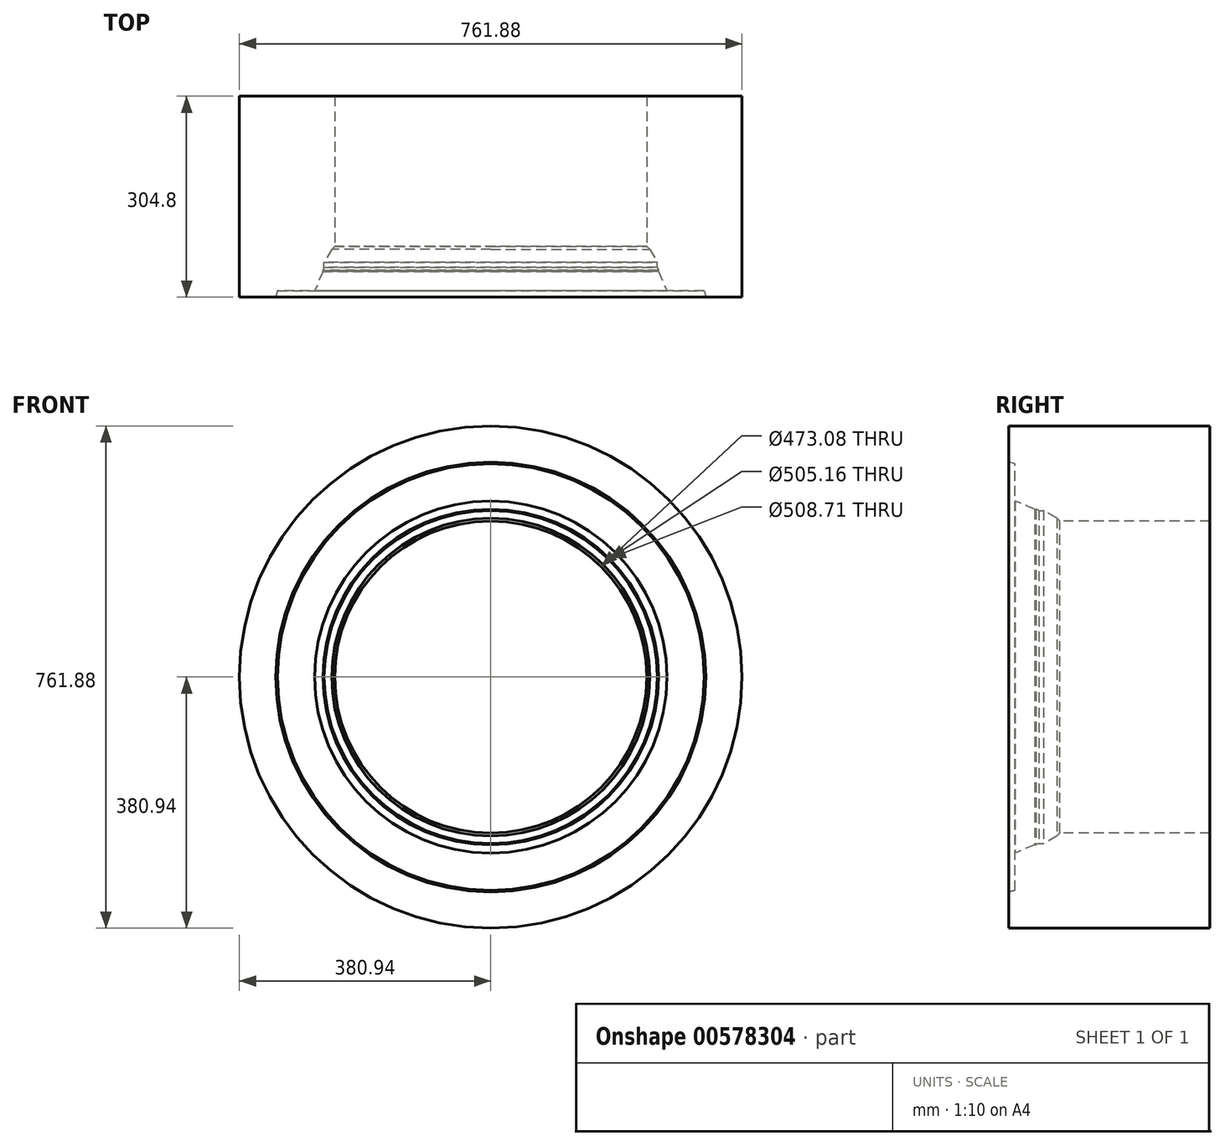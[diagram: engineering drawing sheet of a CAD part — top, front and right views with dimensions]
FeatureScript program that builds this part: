
annotation { "Feature Type Name" : "Feature", "Feature Type Description" : "" }
export const myFeature = defineFeature(function(context is Context, id is Id, definition is map)
    precondition{}
    {
        {
            var Q0;
            Q0=qCreatedBy(makeId("Front.planeOp"),FACE);
            var sketch = newSketch(context, id + "F0", { "sketchPlane" : qUnion([Q0])});
            skCircle(sketch, "E0", {"center": v(0, 0) * mm, "radius": 236.54 * mm});
            skCircle(sketch, "E1", {"center": v(0, 0) * mm, "radius": 380.94 * mm});
            skSolve(sketch);
        }
        {
            var Q0;
            Q0=qSketchRegion(id+"F0",true);
            extrude(context, id + "F1", {"entities" : qUnion([Q0]), "oppositeDirection" : true, "depth" : 304.8 * mm, "offsetDistance" : 25.4 * mm});
        }
        {
            var Q0;
            Q0=qCreatedBy(makeId("Right.planeOp"),FACE);
            var sketch = newSketch(context, id + "F2", { "sketchPlane" : qUnion([Q0])});
            skLineSegment(sketch, "E2", {"start": v(0, 0) * mm, "end": v(-223.81, 0) * mm});
            skPoint(sketch, "E3", {"position": v(0, 325.9) * mm});
            skLineSegment(sketch, "E4", {"start": v(9.52, 323.44) * mm, "end": v(9.53, 0) * mm});
            skLineSegment(sketch, "E5", {"start": v(0, 325.9) * mm, "end": v(9.53, 323.44) * mm});
            skLineSegment(sketch, "E6", {"start": v(0, 0) * mm, "end": v(9.53, 0) * mm});
            skLineSegment(sketch, "E7", {"start": v(0, 325.9) * mm, "end": v(-38.14, 325.9) * mm});
            skLineSegment(sketch, "E8", {"start": v(-38.14, 325.9) * mm, "end": v(0, -5.87) * mm});
            skSolve(sketch);
        }
        {
            var Q0;
            Q0=qSketchRegion(id+"F2",true);
            var Q1;
            Q1=sQuery(id+"F2.wireOp",EDGE,"E2");
            revolve(context, id + "F3", {"operationType" : NewBodyOperationType.REMOVE, "entities" : qUnion([Q0]), "axis" : qUnion([Q1]), "revolveType" : RevolveType.FULL, "oppositeDirection" : true});
        }
        {
            var Q0;
            Q0=qCreatedBy(makeId("Right.planeOp"),FACE);
            var sketch = newSketch(context, id + "F4", { "sketchPlane" : qUnion([Q0])});
            skPoint(sketch, "E9", {"position": v(9.52, 267) * mm});
            skLineSegment(sketch, "E10", {"start": v(9.52, 267) * mm, "end": v(39.3, 254.36) * mm});
            skLineSegment(sketch, "E11", {"start": v(41.25, 254.36) * mm, "end": v(39.3, 254.36) * mm});
            skLineSegment(sketch, "E12", {"start": v(41.25, 254.36) * mm, "end": v(45.44, 252.58) * mm});
            skLineSegment(sketch, "E13", {"start": v(45.44, 252.58) * mm, "end": v(52.7, 252.58) * mm});
            skLineSegment(sketch, "E14", {"start": v(52.7, 252.58) * mm, "end": v(72.8, 240.98) * mm});
            skLineSegment(sketch, "E15", {"start": v(72.8, 240.98) * mm, "end": v(83.79, 229.98) * mm});
            skLineSegment(sketch, "E16", {"start": v(9.52, 267) * mm, "end": v(-83.95, 267) * mm});
            skLineSegment(sketch, "E17", {"start": v(-83.95, 267) * mm, "end": v(-48.08, 188) * mm});
            skLineSegment(sketch, "E18", {"start": v(-48.08, 188) * mm, "end": v(83.79, 229.98) * mm});
            skSolve(sketch);
        }
        {
            var Q0;
            Q0=qSketchRegion(id+"F4",true);
            var Q1;
            Q1=makeQuery(id+"F1.opExtrude","SWEPT_FACE",FACE,{"disambiguationData":[OSD([sQuery(id+"F0.wireOp",EDGE,"E0")])]});
            revolve(context, id + "F5", {"operationType" : NewBodyOperationType.REMOVE, "entities" : qUnion([Q0]), "axis" : qUnion([Q1]), "revolveType" : RevolveType.FULL, "oppositeDirection" : true});
        }
    });
